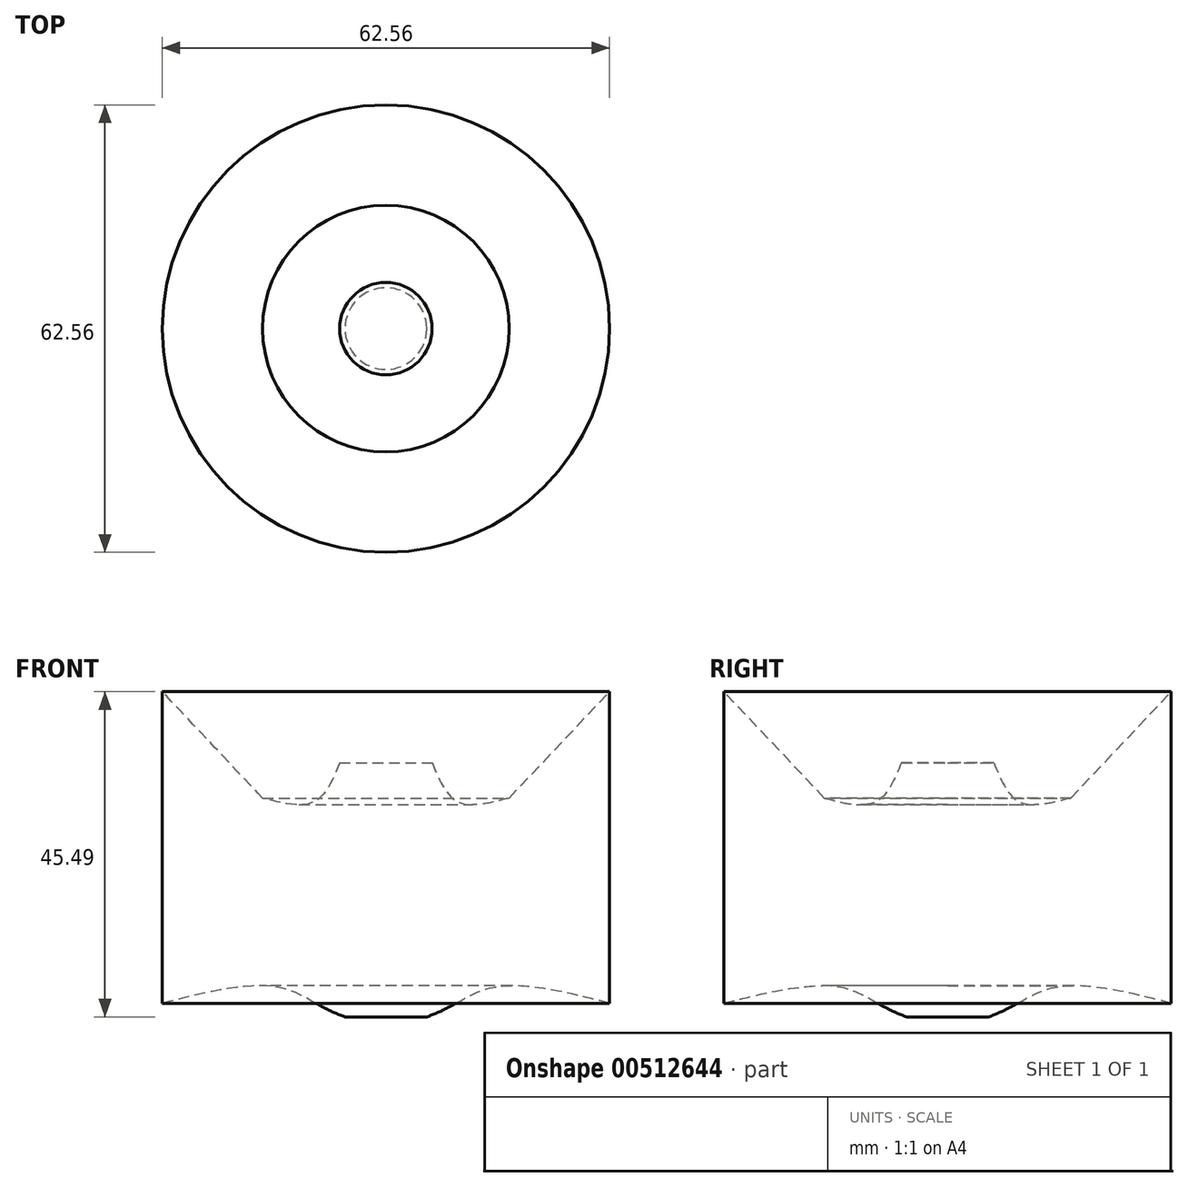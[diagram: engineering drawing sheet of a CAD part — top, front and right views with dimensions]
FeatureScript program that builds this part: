
annotation { "Feature Type Name" : "Feature", "Feature Type Description" : "" }
export const myFeature = defineFeature(function(context is Context, id is Id, definition is map)
    precondition{}
    {
        {
            var Q0;
            Q0=qCreatedBy(makeId("Front.planeOp"),FACE);
            var sketch = newSketch(context, id + "F0", { "sketchPlane" : qUnion([Q0])});
            skLineSegment(sketch, "E0", {"start": v(0, 0) * mm, "end": v(5.71, 0) * mm});
            skFitSpline(sketch, "E1", {"points": [v(5.71, 0) * mm, v(15.47, 4.21) * mm, v(31.28, 1.9) * mm], "startDerivative": vector(27.1, 9.3) * mm, "endDerivative": vector(22.88, -5.84) * mm});
            skLineSegment(sketch, "E2", {"start": v(31.28, 1.9) * mm, "end": v(31.28, 45.5) * mm});
            skLineSegment(sketch, "E3", {"start": v(31.28, 45.5) * mm, "end": v(17.24, 30.6) * mm});
            skLineSegment(sketch, "E4", {"start": v(0, 0) * mm, "end": v(0, 35.56) * mm});
            skLineSegment(sketch, "E5", {"start": v(0, 35.56) * mm, "end": v(6.46, 35.56) * mm});
            skFitSpline(sketch, "E6", {"points": [v(6.46, 35.56) * mm, v(10.06, 30.09) * mm, v(17.24, 30.6) * mm], "startDerivative": vector(5.73, -14.2) * mm, "endDerivative": vector(15.75, 4.13) * mm});
            skSolve(sketch);
        }
        {
            var Q0;
            Q0=makeQuery(id+"F0.imprint","IMPRINT",FACE,{"disambiguationData":[TD([[makeQuery(id+"F0.imprint","IMPRINT",EDGE,{"derivedFrom":sQuery(id+"F0.wireOp",EDGE,"E0")}),1.0]])]});
            var Q1;
            Q1=sQuery(id+"F0.wireOp",EDGE,"E4");
            revolve(context, id + "F1", {"entities" : qUnion([Q0]), "axis" : qUnion([Q1]), "revolveType" : RevolveType.FULL});
        }
    });
